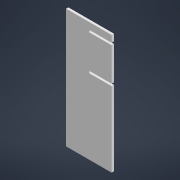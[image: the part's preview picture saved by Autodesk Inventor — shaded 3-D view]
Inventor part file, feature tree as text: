
AUTODESK INVENTOR PART (.ipt)
format: ipt  version: 2021.3 (Build 253353000, 353)  size: 166,400 bytes
history: native  units: in
note: dims shown in document units (in); Inventor stores cm internally (conversion verified against a paired STEP export)
features: extrude x1
ambient origin geometry x8: Origin, YZ Plane, XZ Plane, XY Plane, X Axis, Y Axis, Z Axis, Center Point
bodies: Solid1 (feature_tree)
feature tree (1):
  extrude  "Extrusion1"  Depth=0.23in
